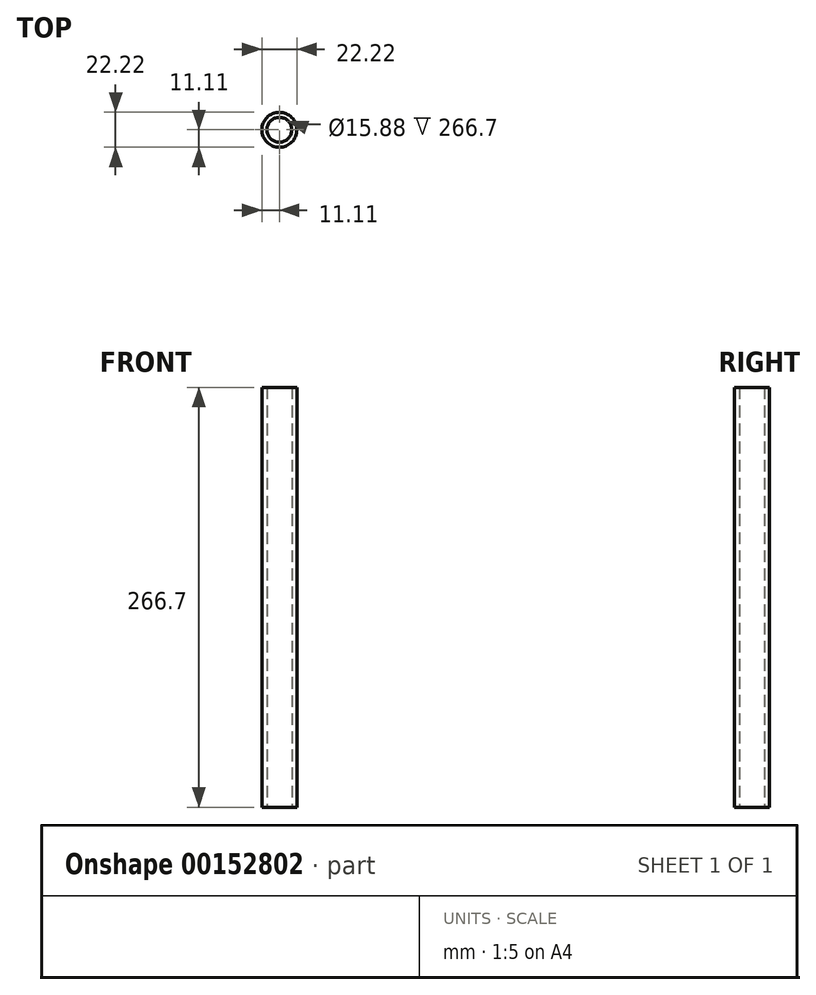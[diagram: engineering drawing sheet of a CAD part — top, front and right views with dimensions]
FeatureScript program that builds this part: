
annotation { "Feature Type Name" : "Feature", "Feature Type Description" : "" }
export const myFeature = defineFeature(function(context is Context, id is Id, definition is map)
    precondition{}
    {
        {
            var Q0;
            Q0=qCreatedBy(makeId("Top.planeOp"),FACE);
            var sketch = newSketch(context, id + "F0", { "sketchPlane" : qUnion([Q0])});
            skCircle(sketch, "E0", {"center": v(0, 0) * mm, "radius": 11.11 * mm});
            skCircle(sketch, "E1", {"center": v(0, 0) * mm, "radius": 7.94 * mm});
            skSolve(sketch);
        }
        {
            var Q0;
            Q0=qSketchRegion(id+"F0",true);
            extrude(context, id + "F1", {"entities" : qUnion([Q0]), "depth" : 266.7 * mm});
        }
    });
